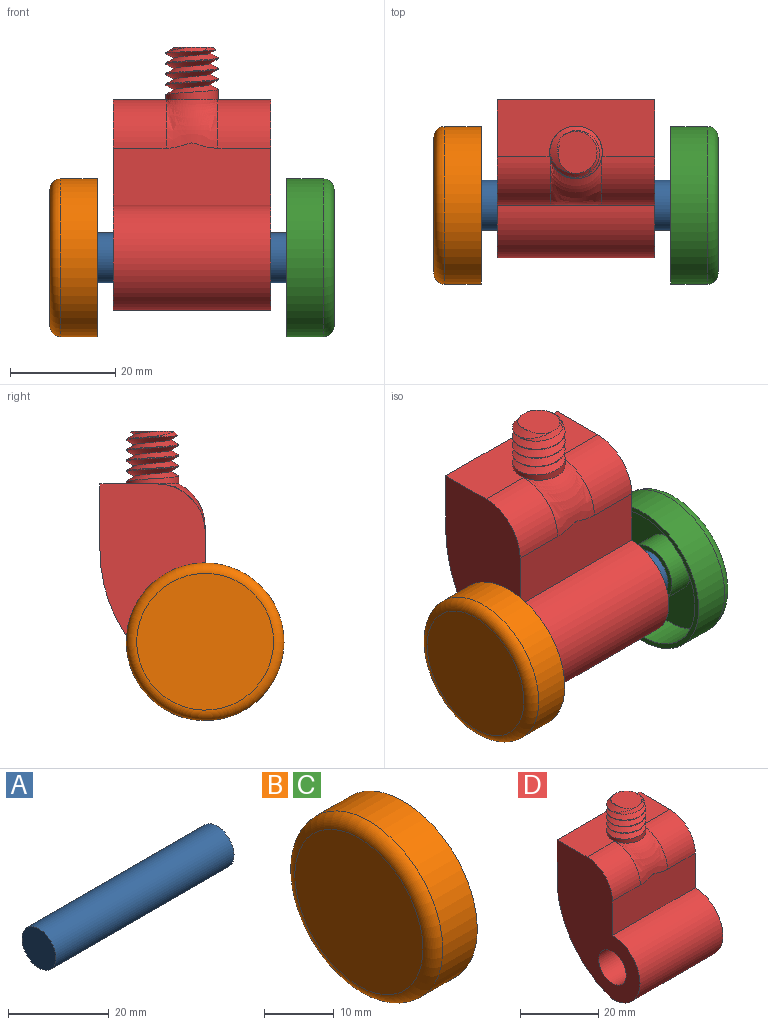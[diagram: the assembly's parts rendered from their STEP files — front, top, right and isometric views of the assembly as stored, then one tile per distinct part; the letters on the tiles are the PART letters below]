
ASSEMBLY  parts=4 mates=3
PART A: 3 faces, bbox 50x9.5x9.5 mm
  f0: cylinder r=4.75mm len=50mm, axis (-1,0,0), area 1492.3mm2, adj f1,f2
  f1: plane 9.5x9.5mm, normal (1,0,0), area 70.9mm2, adj f0
  f2: plane 9.5x9.5mm, normal (-1,0,0), area 70.9mm2, adj f0
PART B: 10 faces, bbox 9x32.5x32.5 mm
  f0: cylinder r=14mm len=28mm, axis (-1,0,0), area 615.8mm2, adj f2,f4
  f1: cylinder r=15mm len=30mm, axis (-1,0,0), area 659.7mm2, adj f2,f9
  f2: plane 30x30mm, normal (1,0,0), area 91.1mm2, adj f0,f1
  f3: plane 26x26mm, normal (-1,0,0), area 530.9mm2, adj f9
  f4: plane 28x28mm, normal (1,0,0), area 511.9mm2, adj f0,f6
  f5: cylinder r=4.75mm len=9.5mm, axis (-1,0,0), area 149.2mm2, adj f7,f8
  f6: cylinder r=5.75mm len=11.5mm, axis (-1,0,0), area 180.6mm2, adj f4,f7
  f7: plane 11.5x11.5mm, normal (1,0,0), area 33mm2, adj f5,f6
  f8: plane 9.5x9.5mm, normal (1,0,0), area 70.9mm2, adj f5
  f9: torus R=13mm, axis (1,0,0), area 281.7mm2, adj f1,f3
PART C: same geometry as B
PART D: 17 faces, bbox 30.2x30.2x51.4 mm
  f0: cylinder r=5mm len=10mm, axis (0,0,-1), area 48.3mm2, adj f4,f9,f11,f14,f15,f16
  f1: plane 30x11.83mm, normal (0,-1,0), area 328.7mm2, adj f2,f6,f7,f10,f11,f12
  f2: cylinder r=10mm len=30mm, axis (-1,0,0), area 942.5mm2, adj f1,f6,f7,f13
  f3: plane 30x12.63mm, normal (0,1,0), area 378.9mm2, adj f4,f6,f7,f13
  f4: plane 30x10.83mm, normal (0,0,1), area 277.3mm2, adj f0,f3,f6,f7,f10,f12
  f5: cylinder r=5mm len=30mm, axis (-1,0,0), area 942.5mm2, adj f6,f7
  f6: plane 40x30mm, normal (1,0,0), area 714.4mm2, adj f1,f2,f3,f4,f5,f12,f13
  f7: plane 40x30mm, normal (-1,0,0), area 714.4mm2, adj f1,f2,f3,f4,f5,f10,f13
  f8: plane 8.23x7.8mm, normal (0,0,1), area 47.8mm2, adj f9,f15,f16
  f9: cone r=4mm half-angle=45deg, axis (0,0,-1), area 14.1mm2, adj f0,f8,f15,f16
  f10: cylinder r=9.17mm len=10.07mm, axis (-1,0,0), area 145.1mm2, adj f1,f4,f7,f11
  f11: bspline ~11.49x9.34mm, area 113.2mm2, adj f0,f1,f10,f12
  f12: cylinder r=9.17mm len=10.07mm, axis (-1,0,0), area 145.1mm2, adj f1,f4,f6,f11
  f13: cylinder r=28.73mm len=30mm, axis (-1,0,0), area 1087.7mm2, adj f2,f3,f6,f7
  f14: plane 1.85x1.6mm, normal (0,1,0), area 1.5mm2, adj f0,f15,f16
  f15: bspline ~11.55x10.26mm, area 201.4mm2, adj f0,f8,f9,f14,f16
  f16: bspline ~11.55x10.59mm, area 225.9mm2, adj f0,f8,f9,f14,f15
PLACE A rot(axis=(-1,0,0),116deg) t=(-27.1,-10.13,-7.65)mm
PLACE B rot(axis=(-1,0,0),26deg) t=(-29.1,-10.13,-7.65)mm
PLACE C rot(axis=(0,0.23,0.97),180deg) t=(24.9,-10.13,-7.65)mm
PLACE D t=(-17.1,-10.13,-7.65)mm fixed
MATE revolute A.f0 <-> D.f2  axis (-1,0,0) through (-2.1,-10.13,-7.65)mm
MATE fastened C.f5 <-> A.f0  axis (-1,0,0) through (22.9,-10.13,-7.65)mm
MATE fastened B.f5 <-> A.f0  axis (1,0,0) through (-27.1,-10.13,-7.65)mm
